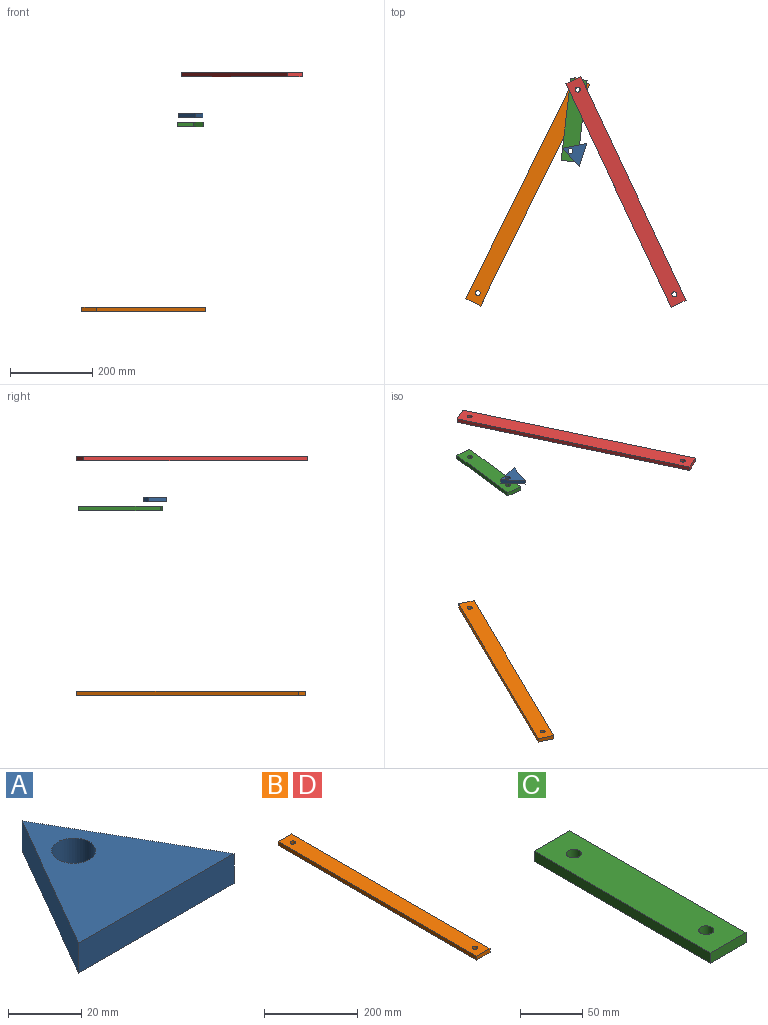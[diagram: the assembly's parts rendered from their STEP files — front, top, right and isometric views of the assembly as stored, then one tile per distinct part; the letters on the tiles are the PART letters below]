
ASSEMBLY  parts=4 mates=4
PART A: 6 faces, bbox 60x52x10 mm
  f0: plane 51.96x30mm, normal (-0.87,0.5,0), area 600mm2, adj f1,f2,f4,f5
  f1: plane 60x10mm, normal (0,-1,0), area 600mm2, adj f0,f2,f4,f5
  f2: plane 51.96x30mm, normal (0.87,0.5,0), area 600mm2, adj f0,f1,f4,f5
  f3: cylinder r=6mm len=12mm, axis (0,0,-1), area 377mm2, adj f4,f5
  f4: plane 60x51.96mm, normal (0,0,1), area 1445.7mm2, adj f0,f1,f2,f3
  f5: plane 60x51.96mm, normal (0,0,-1), area 1445.7mm2, adj f0,f1,f2,f3
PART B: 8 faces, bbox 40x600x10 mm
  f0: plane 40x10mm, normal (0,-1,0), area 400mm2, adj f1,f5,f6,f7
  f1: plane 600x10mm, normal (1,0,0), area 6000mm2, adj f0,f2,f6,f7
  f2: plane 40x10mm, normal (0,1,0), area 400mm2, adj f1,f5,f6,f7
  f3: cylinder r=6mm len=12mm, axis (0,0,-1), area 377mm2, adj f6,f7
  f4: cylinder r=6mm len=12mm, axis (0,0,-1), area 377mm2, adj f6,f7
  f5: plane 600x10mm, normal (-1,0,0), area 6000mm2, adj f0,f2,f6,f7
  f6: plane 600x40mm, normal (0,0,1), area 23773.8mm2, adj f0,f1,f2,f3,f4,f5
  f7: plane 600x40mm, normal (0,0,-1), area 23773.8mm2, adj f0,f1,f2,f3,f4,f5
PART C: 8 faces, bbox 40x200x10 mm
  f0: plane 40x10mm, normal (0,-1,0), area 400mm2, adj f1,f5,f6,f7
  f1: plane 200x10mm, normal (1,0,0), area 2000mm2, adj f0,f2,f6,f7
  f2: plane 40x10mm, normal (0,1,0), area 400mm2, adj f1,f5,f6,f7
  f3: cylinder r=6mm len=12mm, axis (0,0,-1), area 377mm2, adj f6,f7
  f4: cylinder r=6mm len=12mm, axis (0,0,-1), area 377mm2, adj f6,f7
  f5: plane 200x10mm, normal (-1,0,0), area 2000mm2, adj f0,f2,f6,f7
  f6: plane 200x40mm, normal (0,0,1), area 7773.8mm2, adj f0,f1,f2,f3,f4,f5
  f7: plane 200x40mm, normal (0,0,-1), area 7773.8mm2, adj f0,f1,f2,f3,f4,f5
PART D: same geometry as B
PLACE A rot(axis=(0,0,1),71.4deg) t=(-19.15,50.19,-5)mm fixed
PLACE B rot(axis=(0,0,-1),26.2deg) t=(-153.26,-37.39,-475.55)mm
PLACE C rot(axis=(0,0,-1),6.7deg) t=(-40.63,134.87,-26.93)mm
PLACE D rot(axis=(0,0,1),25.3deg) t=(85.53,-39.36,93.71)mm
MATE cylindrical C.f4 <-> B.f4  axis (0,0,1) through (-31.82,209.35,-16.93)mm
MATE parallel D.f4 <-> C.f4  axis (0,0,-1) through (-31.82,209.35,98.71)mm
MATE cylindrical C.f3 <-> A.f3  axis (0,0,1) through (-49.44,60.39,-16.93)mm
MATE cylindrical D.f4 <-> C.f4  axis (0,0,1) through (-31.82,209.35,103.71)mm
